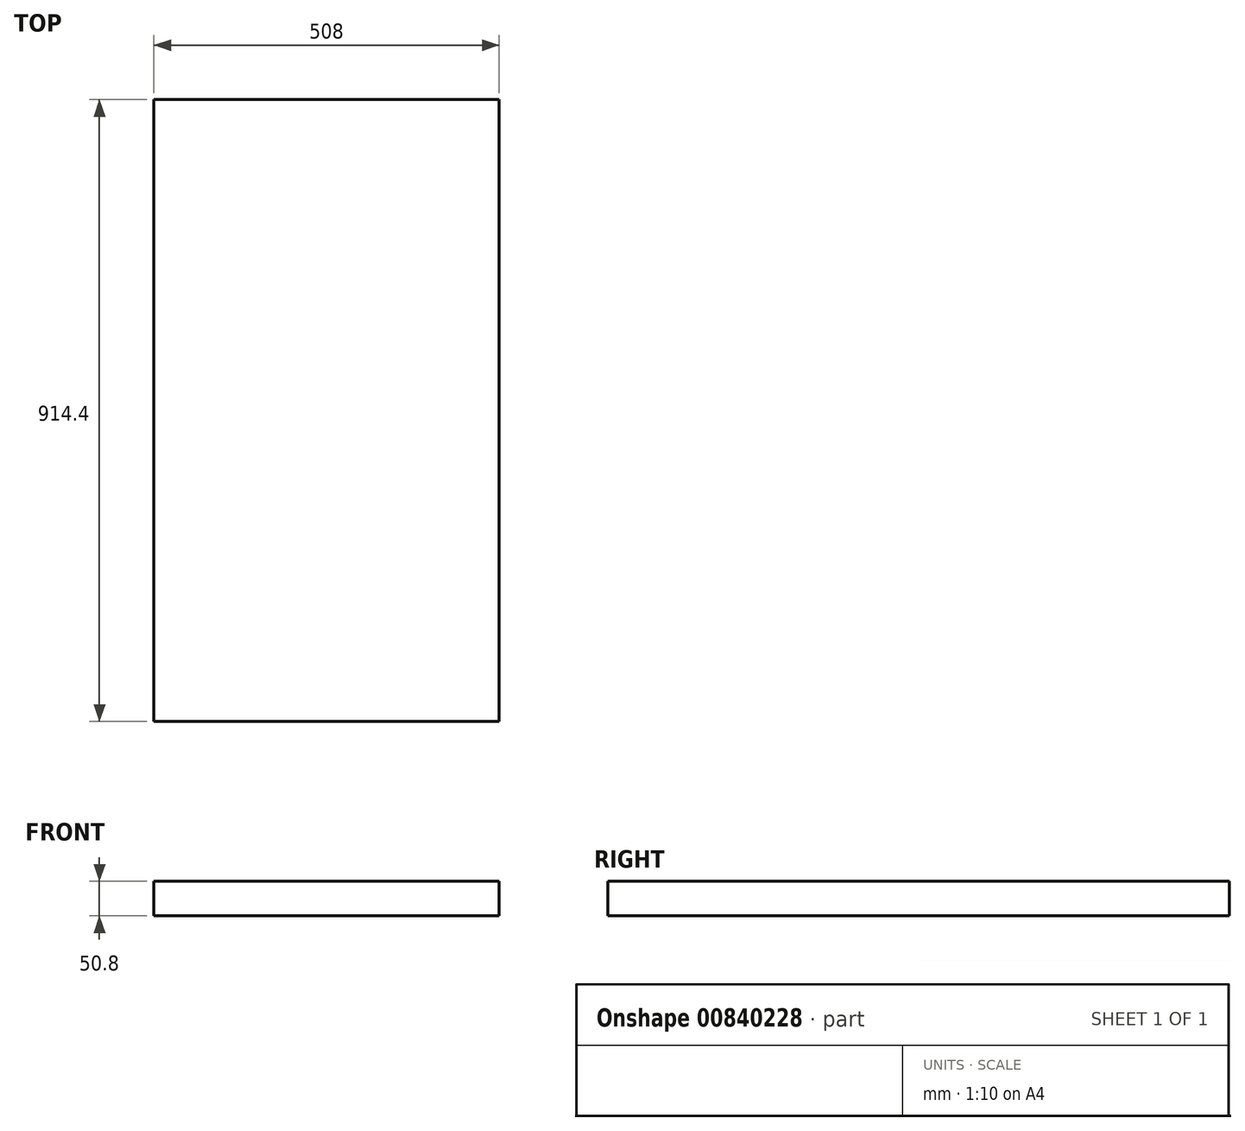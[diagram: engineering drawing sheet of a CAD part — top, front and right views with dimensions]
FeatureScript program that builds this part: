
annotation { "Feature Type Name" : "Feature", "Feature Type Description" : "" }
export const myFeature = defineFeature(function(context is Context, id is Id, definition is map)
    precondition{}
    {
        {
            var Q0;
            Q0=qCreatedBy(makeId("Top.planeOp"),FACE);
            var sketch = newSketch(context, id + "F0", { "sketchPlane" : qUnion([Q0])});
            skLineSegment(sketch, "E0.bottom", {"start": v(0, 0) * mm, "end": v(508, 0) * mm});
            skLineSegment(sketch, "E0.top", {"start": v(0, 914.4) * mm, "end": v(508, 914.4) * mm});
            skLineSegment(sketch, "E0.left", {"start": v(0, 0) * mm, "end": v(0, 914.4) * mm});
            skLineSegment(sketch, "E0.right", {"start": v(508, 0) * mm, "end": v(508, 914.4) * mm});
            skSolve(sketch);
        }
        {
            var Q0;
            Q0 = qSketchRegion(id + "F0", true);
            extrude(context, id + "F1", {"entities" : qUnion([Q0]), "depth" : 50.8 * mm, "offsetDistance" : 25.4 * mm});
        }
    });
